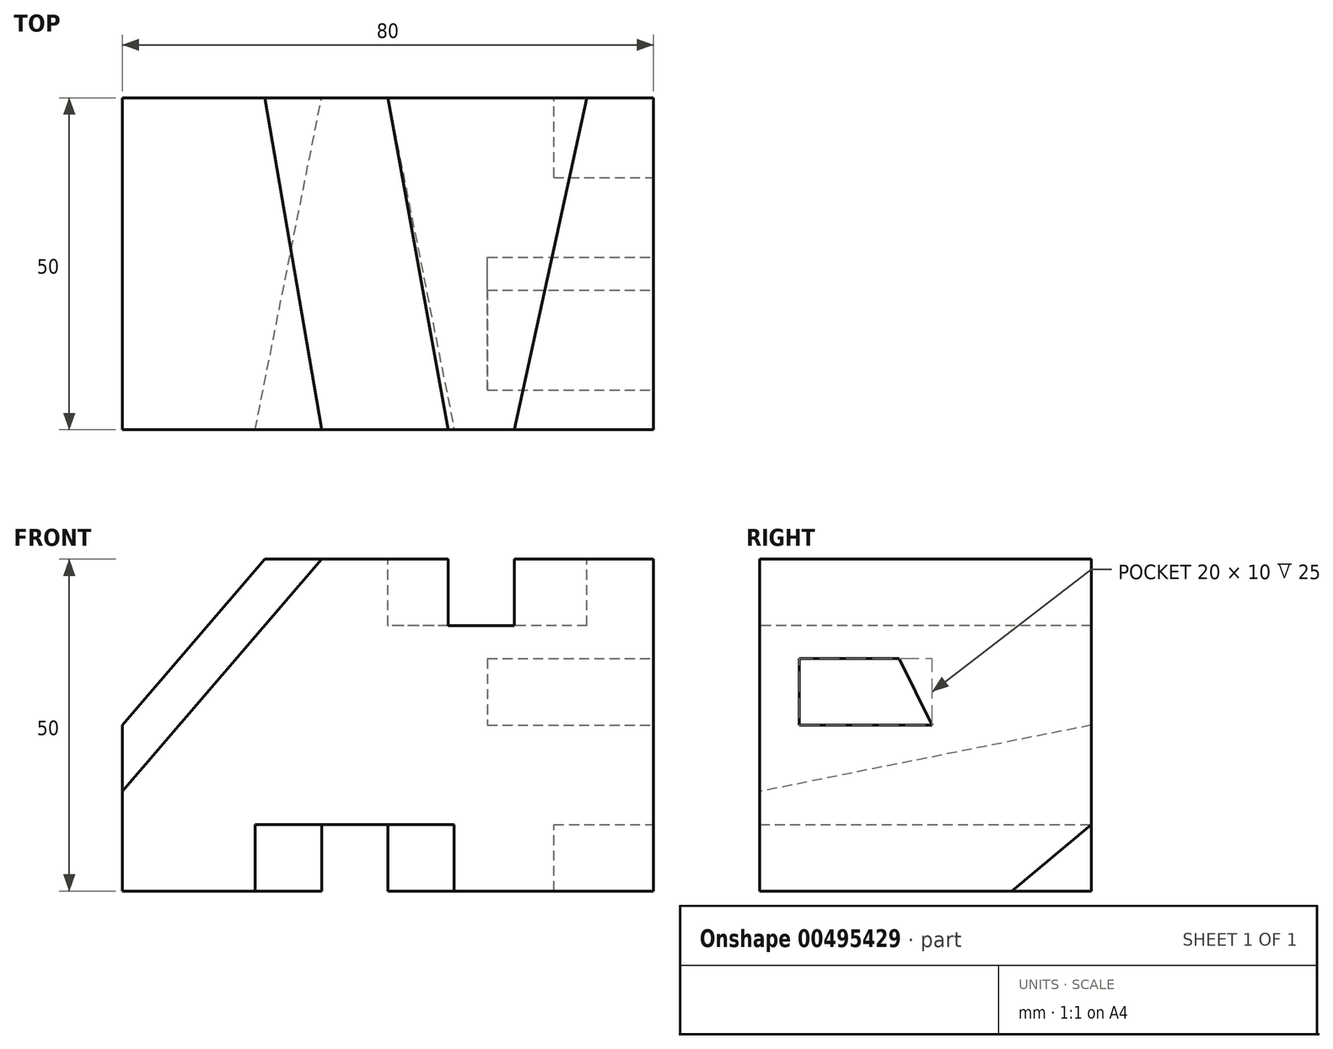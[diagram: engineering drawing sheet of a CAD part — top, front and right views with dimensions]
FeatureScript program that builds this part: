
annotation { "Feature Type Name" : "Feature", "Feature Type Description" : "" }
export const myFeature = defineFeature(function(context is Context, id is Id, definition is map)
    precondition{}
    {
        {
            var Q0;
            Q0=qCreatedBy(makeId("Front.planeOp"),FACE);
            var sketch = newSketch(context, id + "F0", { "sketchPlane" : qUnion([Q0])});
            skLineSegment(sketch, "E0.bottom", {"start": v(0, 0) * mm, "end": v(-80, 0) * mm});
            skLineSegment(sketch, "E0.top", {"start": v(0, 50) * mm, "end": v(-80, 50) * mm});
            skLineSegment(sketch, "E0.left", {"start": v(0, 0) * mm, "end": v(0, 50) * mm});
            skLineSegment(sketch, "E0.right", {"start": v(-80, 0) * mm, "end": v(-80, 50) * mm});
            skSolve(sketch);
        }
        {
            var Q0;
            Q0 = qSketchRegion(id + "F0", true);
            extrude(context, id + "F1", {"entities" : qUnion([Q0]), "depth" : 50 * mm});
        }
        {
            var Q0;
            Q0=makeQuery(id+"F1.opExtrude","SWEPT_FACE",FACE,{"disambiguationData":[OSD([sQuery(id+"F0.wireOp",EDGE,"E0.top")])]});
            var sketch = newSketch(context, id + "F2", { "sketchPlane" : qUnion([Q0])});
            skLineSegment(sketch, "E1", {"start": v(-80, 0) * mm, "end": v(-60, 0) * mm});
            skLineSegment(sketch, "E2", {"start": v(-60, 0) * mm, "end": v(-50, -50) * mm});
            skLineSegment(sketch, "E3", {"start": v(-50, -50) * mm, "end": v(-80, -50) * mm});
            skSolve(sketch);
        }
        {
            var Q0;
            Q0=makeQuery(id+"F1.opExtrude","CAP_FACE",FACE,{"disambiguationData":[OSD([sQuery(id+"F0.wireOp",EDGE,"E0.bottom"),sQuery(id+"F0.wireOp",EDGE,"E0.top"),sQuery(id+"F0.wireOp",EDGE,"E0.left"),sQuery(id+"F0.wireOp",EDGE,"E0.right")])],"isStart":false});
            var sketch = newSketch(context, id + "F3", { "sketchPlane" : qUnion([Q0])});
            skLineSegment(sketch, "E4", {"start": v(-80, 0) * mm, "end": v(-80, 15) * mm});
            skLineSegment(sketch, "E5", {"start": v(-80, 50) * mm, "end": v(-50, 50) * mm});
            skLineSegment(sketch, "E6", {"start": v(-50, 50) * mm, "end": v(-80, 15) * mm});
            skSolve(sketch);
        }
        {
            var Q0;
            Q0=makeQuery(id+"F1.opExtrude","SWEPT_FACE",FACE,{"disambiguationData":[OSD([sQuery(id+"F0.wireOp",EDGE,"E0.right")])]});
            var sketch = newSketch(context, id + "F4", { "sketchPlane" : qUnion([Q0])});
            skLineSegment(sketch, "E7", {"start": v(50, 0) * mm, "end": v(50, 15) * mm});
            skLineSegment(sketch, "E8", {"start": v(0, 0) * mm, "end": v(0, 25) * mm});
            skLineSegment(sketch, "E9", {"start": v(0, 25) * mm, "end": v(50, 15) * mm});
            skSolve(sketch);
        }
        {
            var Q0;
            Q0=makeQuery(id+"F2.imprint","IMPRINT",FACE,{"disambiguationData":[TD([[makeQuery(id+"F2.imprint","IMPRINT",EDGE,{"derivedFrom":sQuery(id+"F2.wireOp",EDGE,"E1")}),1.0]])]});
            var Q1;
            {var subQ0=sQuery(id+"F4.wireOp",EDGE,"E9");Q1=makeQuery(id+"F4.imprint","IMPRINT",FACE,{"disambiguationData":[TD([[makeQuery(id+"F4.imprint","IMPRINT",EDGE,{"derivedFrom":subQ0}),1.0]])]});}
            var Q2;
            Q2=sQuery(id+"F3.wireOp",EDGE,"E6");
            sweep(context, id + "F5", {"operationType" : NewBodyOperationType.REMOVE, "profiles" : qUnion([Q0, Q1]), "path" : qUnion([Q2])});
        }
        {
            var Q0;
            Q0=makeQuery(id+"F1.opExtrude","SWEPT_FACE",FACE,{"disambiguationData":[OSD([sQuery(id+"F0.wireOp",EDGE,"E0.top")])]});
            var sketch = newSketch(context, id + "F6", { "sketchPlane" : qUnion([Q0])});
            skLineSegment(sketch, "E10", {"start": v(0, 0) * mm, "end": v(-10, 0) * mm});
            skLineSegment(sketch, "E11", {"start": v(-10, 0) * mm, "end": v(-20.93, -50) * mm});
            skLineSegment(sketch, "E12", {"start": v(-20.93, -50) * mm, "end": v(-30.93, -50) * mm});
            skLineSegment(sketch, "E13", {"start": v(-30.93, -50) * mm, "end": v(-40, 0) * mm});
            skLineSegment(sketch, "E14", {"start": v(-40, 0) * mm, "end": v(-60, 0) * mm});
            skLineSegment(sketch, "E15", {"start": v(-40, 0) * mm, "end": v(-10, 0) * mm});
            skSolve(sketch);
        }
        {
            var Q0;
            Q0=makeQuery(id+"F6.imprint","IMPRINT",FACE,{"disambiguationData":[TD([[makeQuery(id+"F6.imprint","IMPRINT",EDGE,{"derivedFrom":sQuery(id+"F6.wireOp",EDGE,"E11")}),-1.0]])]});
            extrude(context, id + "F7", {"entities" : qUnion([Q0]), "operationType" : NewBodyOperationType.REMOVE, "oppositeDirection" : true, "depth" : 10 * mm});
        }
        {
            var Q0;
            Q0=makeQuery(id+"F1.opExtrude","SWEPT_FACE",FACE,{"disambiguationData":[OSD([sQuery(id+"F0.wireOp",EDGE,"E0.bottom")])]});
            var sketch = newSketch(context, id + "F8", { "sketchPlane" : qUnion([Q0])});
            skLineSegment(sketch, "E16", {"start": v(-80, 50) * mm, "end": v(-60, 50) * mm});
            skLineSegment(sketch, "E17", {"start": v(-60, 50) * mm, "end": v(-50, 0) * mm});
            skLineSegment(sketch, "E18", {"start": v(-50, 0) * mm, "end": v(-40, 0) * mm});
            skLineSegment(sketch, "E19", {"start": v(-40, 0) * mm, "end": v(-30, 50) * mm});
            skLineSegment(sketch, "E20", {"start": v(-30, 50) * mm, "end": v(-60, 50) * mm});
            skLineSegment(sketch, "E21", {"start": v(-50, 0) * mm, "end": v(-80, 0) * mm});
            skSolve(sketch);
        }
        {
            var Q0;
            Q0 = qSketchRegion(id + "F8", true);
            extrude(context, id + "F9", {"entities" : qUnion([Q0]), "operationType" : NewBodyOperationType.REMOVE, "oppositeDirection" : true, "depth" : 10 * mm});
        }
        {
            var Q0;
            Q0=makeQuery(id+"F1.opExtrude","SWEPT_FACE",FACE,{"disambiguationData":[OSD([sQuery(id+"F0.wireOp",EDGE,"E0.left")])]});
            var sketch = newSketch(context, id + "F10", { "sketchPlane" : qUnion([Q0])});
            skLineSegment(sketch, "E22", {"start": v(-50, 50) * mm, "end": v(-44, 50) * mm});
            skLineSegment(sketch, "E23", {"start": v(-44, 50) * mm, "end": v(-44, 35) * mm});
            skLineSegment(sketch, "E24", {"start": v(-44, 35) * mm, "end": v(-44, 25) * mm});
            skLineSegment(sketch, "E25", {"start": v(-44, 25) * mm, "end": v(-24, 25) * mm});
            skLineSegment(sketch, "E26", {"start": v(-24, 25) * mm, "end": v(-24, 35) * mm});
            skLineSegment(sketch, "E27", {"start": v(-24, 35) * mm, "end": v(-29, 35) * mm});
            skLineSegment(sketch, "E28", {"start": v(-29, 35) * mm, "end": v(-44, 35) * mm});
            skLineSegment(sketch, "E29", {"start": v(-29, 35) * mm, "end": v(-24, 25) * mm});
            skSolve(sketch);
        }
        {
            var Q0;
            Q0=makeQuery(id+"F10.imprint","IMPRINT",FACE,{"disambiguationData":[TD([[makeQuery(id+"F10.imprint","IMPRINT",EDGE,{"derivedFrom":sQuery(id+"F10.wireOp",EDGE,"E24")}),1.0]])]});
            extrude(context, id + "F11", {"entities" : qUnion([Q0]), "operationType" : NewBodyOperationType.REMOVE, "oppositeDirection" : true, "depth" : 25 * mm});
        }
        {
            var Q0;
            Q0=makeQuery(id+"F1.opExtrude","SWEPT_FACE",FACE,{"disambiguationData":[OSD([sQuery(id+"F0.wireOp",EDGE,"E0.left")])]});
            var sketch = newSketch(context, id + "F12", { "sketchPlane" : qUnion([Q0])});
            skLineSegment(sketch, "E30", {"start": v(0, 0) * mm, "end": v(-12, 0) * mm});
            skLineSegment(sketch, "E31", {"start": v(-12, 0) * mm, "end": v(0, 10) * mm});
            skLineSegment(sketch, "E32", {"start": v(0, 10) * mm, "end": v(0, 0) * mm});
            skSolve(sketch);
        }
        {
            var Q0;
            Q0 = qSketchRegion(id + "F12", true);
            extrude(context, id + "F13", {"entities" : qUnion([Q0]), "operationType" : NewBodyOperationType.REMOVE, "oppositeDirection" : true, "depth" : 15 * mm});
        }
    });
